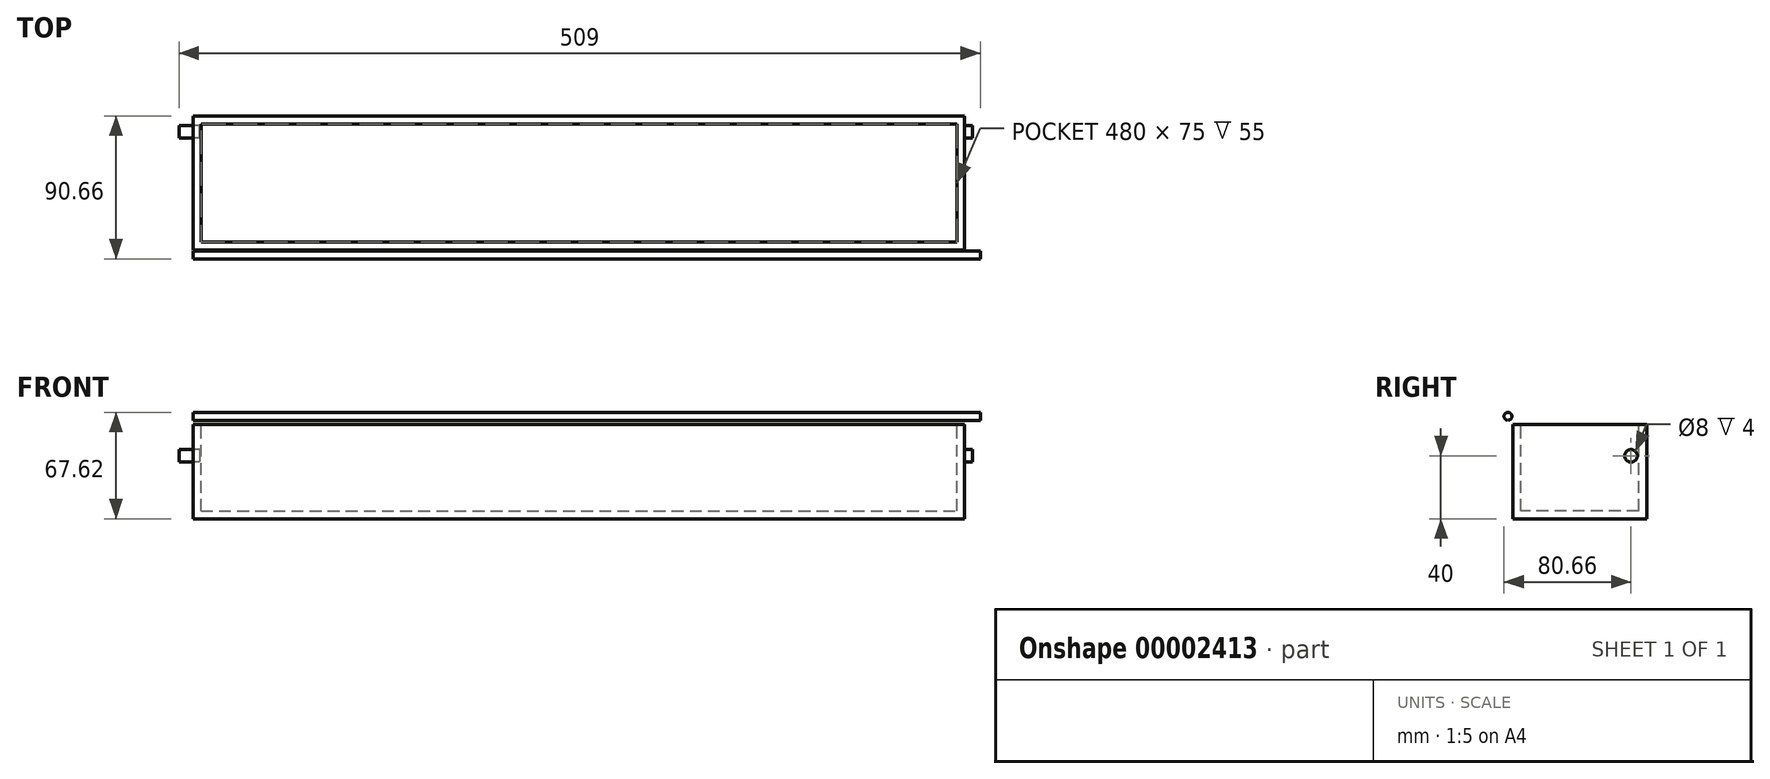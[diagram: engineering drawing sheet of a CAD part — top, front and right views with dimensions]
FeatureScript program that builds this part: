
annotation { "Feature Type Name" : "Feature", "Feature Type Description" : "" }
export const myFeature = defineFeature(function(context is Context, id is Id, definition is map)
    precondition{}
    {
        {
            var Q0;
            Q0=qCreatedBy(makeId("Right.planeOp"),FACE);
            var sketch = newSketch(context, id + "F0", { "sketchPlane" : qUnion([Q0])});
            skCircle(sketch, "E0", {"center": v(-3.16, 5.12) * mm, "radius": 2.5 * mm});
            skSolve(sketch);
        }
        {
            var Q0;
            Q0=makeQuery(id+"F0.imprint","IMPRINT",FACE,{"disambiguationData":[TD([[makeQuery(id+"F0.imprint","IMPRINT",EDGE,{"derivedFrom":sQuery(id+"F0.wireOp",EDGE,"E0")}),1.0]])]});
            extrude(context, id + "F1", {"entities" : qUnion([Q0]), "depth" : 500 * mm});
        }
        {
            var Q0;
            Q0=qCreatedBy(makeId("Top.planeOp"),FACE);
            var sketch = newSketch(context, id + "F2", { "sketchPlane" : qUnion([Q0])});
            skLineSegment(sketch, "E1.bottom", {"start": v(0, 0) * mm, "end": v(490, 0) * mm});
            skLineSegment(sketch, "E1.top", {"start": v(0, 85) * mm, "end": v(490, 85) * mm});
            skLineSegment(sketch, "E1.left", {"start": v(0, 85) * mm, "end": v(0, 0) * mm});
            skLineSegment(sketch, "E1.right", {"start": v(490, 85) * mm, "end": v(490, 0) * mm});
            skLineSegment(sketch, "E2.0", {"start": v(5, 80) * mm, "end": v(485, 80) * mm});
            skLineSegment(sketch, "E2.1", {"start": v(5, 80) * mm, "end": v(5, 5) * mm});
            skLineSegment(sketch, "E2.2", {"start": v(5, 5) * mm, "end": v(485, 5) * mm});
            skLineSegment(sketch, "E2.3", {"start": v(485, 80) * mm, "end": v(485, 5) * mm});
            skSolve(sketch);
        }
        {
            var Q0;
            Q0=makeQuery(id+"F2.imprint","IMPRINT",FACE,{"disambiguationData":[TD([[makeQuery(id+"F2.imprint","IMPRINT",EDGE,{"derivedFrom":sQuery(id+"F2.wireOp",EDGE,"E2.0")}),-1.0]])]});
            var Q1;
            Q1=makeQuery(id+"F2.imprint","IMPRINT",FACE,{"disambiguationData":[TD([[makeQuery(id+"F2.imprint","IMPRINT",EDGE,{"derivedFrom":sQuery(id+"F2.wireOp",EDGE,"E1.bottom")}),1.0]])]});
            extrude(context, id + "F3", {"entities" : qUnion([Q0, Q1]), "oppositeDirection" : true, "depth" : 60 * mm});
        }
        {
            var Q0;
            Q0=makeQuery(id+"F2.imprint","IMPRINT",FACE,{"disambiguationData":[TD([[makeQuery(id+"F2.imprint","IMPRINT",EDGE,{"derivedFrom":sQuery(id+"F2.wireOp",EDGE,"E2.0")}),-1.0]])]});
            extrude(context, id + "F4", {"entities" : qUnion([Q0]), "operationType" : NewBodyOperationType.REMOVE, "oppositeDirection" : true, "depth" : 55 * mm});
        }
        {
            var Q0;
            Q0=makeQuery(id+"F3.opExtrude","SWEPT_FACE",FACE,{"disambiguationData":[OSD([sQuery(id+"F2.wireOp",EDGE,"E1.right")])]});
            var sketch = newSketch(context, id + "F5", { "sketchPlane" : qUnion([Q0])});
            skCircle(sketch, "E3", {"center": v(75, -20) * mm, "radius": 4 * mm});
            skSolve(sketch);
        }
        {
            var Q0;
            Q0=makeQuery(id+"F5.imprint","IMPRINT",FACE,{"disambiguationData":[TD([[makeQuery(id+"F5.imprint","IMPRINT",EDGE,{"derivedFrom":sQuery(id+"F5.wireOp",EDGE,"E3")}),1.0]])]});
            extrude(context, id + "F6", {"entities" : qUnion([Q0]), "operationType" : NewBodyOperationType.ADD, "depth" : 5 * mm});
        }
        {
            var Q0;
            Q0=makeQuery(id+"F3.opExtrude","SWEPT_FACE",FACE,{"disambiguationData":[OSD([sQuery(id+"F2.wireOp",EDGE,"E1.left")])]});
            var sketch = newSketch(context, id + "F7", { "sketchPlane" : qUnion([Q0])});
            skCircle(sketch, "E4", {"center": v(-75, -20) * mm, "radius": 4 * mm});
            skSolve(sketch);
        }
        {
            var Q0;
            Q0 = qSketchRegion(id + "F7", true);
            var Q1;
            Q1=makeQuery(id+"F4.boolean.opBoolean","COPY",FACE,{"derivedFrom":makeQuery(id+"F4.opExtrude","SWEPT_FACE",FACE,{"disambiguationData":[OSD([sQuery(id+"F2.wireOp",EDGE,"E2.1")])]})});
            extrude(context, id + "F8", {"entities" : qUnion([Q0]), "operationType" : NewBodyOperationType.REMOVE, "oppositeDirection" : true, "endBoundEntity" : qUnion([Q1]), "depth" : 4 * mm});
        }
        {
            var Q0;
            Q0 = qSketchRegion(id + "F7", true);
            extrude(context, id + "F9", {"entities" : qUnion([Q0]), "depth" : 9 * mm});
        }
    });
